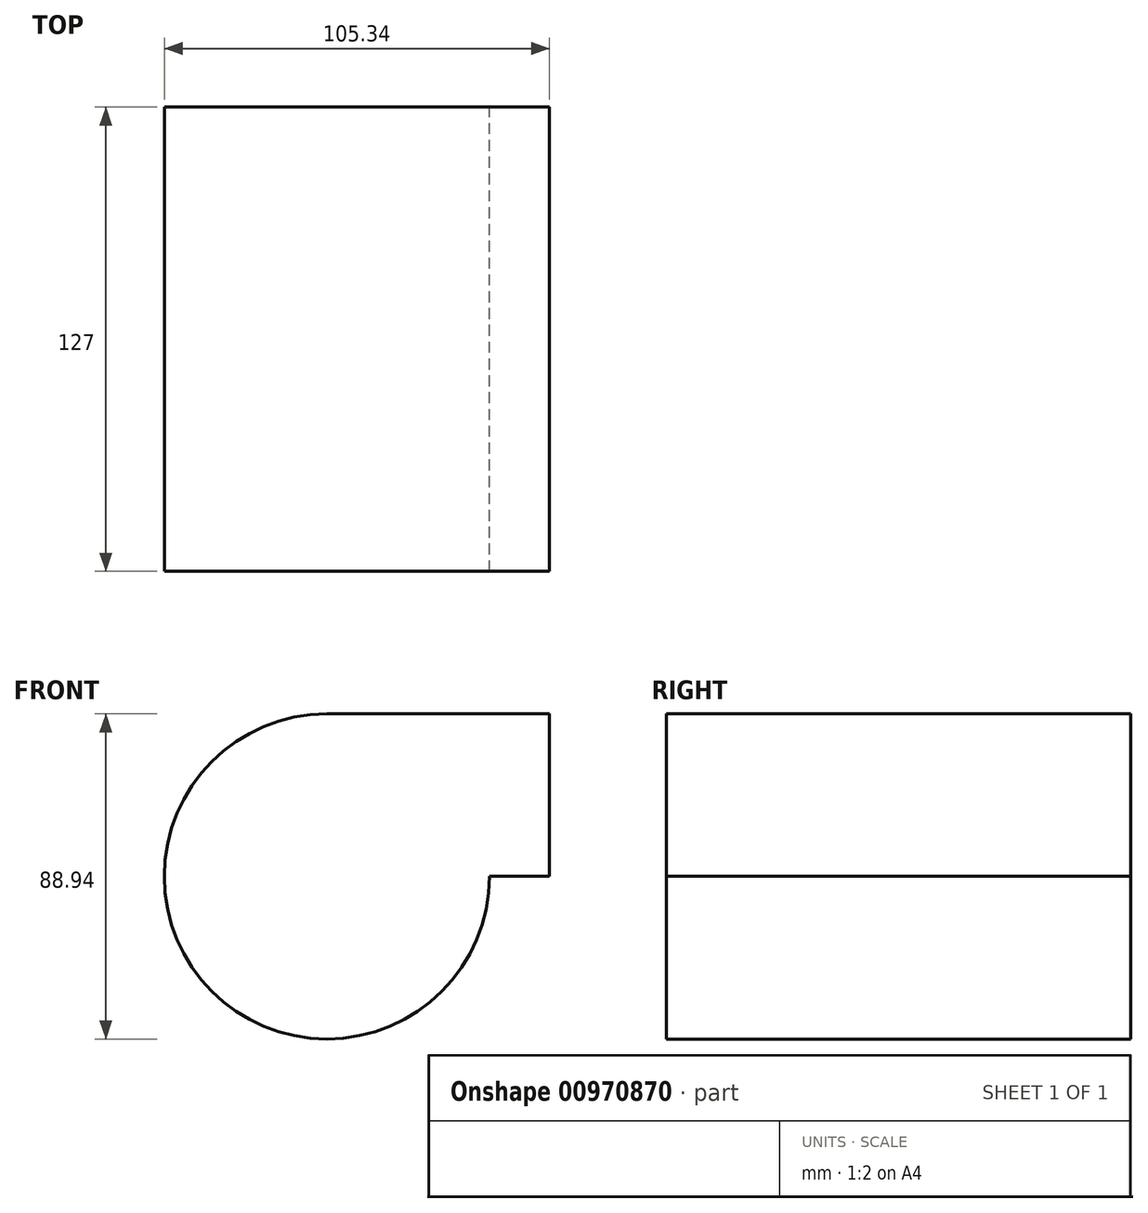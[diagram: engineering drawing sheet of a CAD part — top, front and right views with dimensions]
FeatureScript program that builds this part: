
annotation { "Feature Type Name" : "Feature", "Feature Type Description" : "" }
export const myFeature = defineFeature(function(context is Context, id is Id, definition is map)
    precondition{}
    {
        {
            var Q0;
            Q0=qCreatedBy(makeId("Front.planeOp"),FACE);
            var sketch = newSketch(context, id + "F0", { "sketchPlane" : qUnion([Q0])});
            skLineSegment(sketch, "E0", {"start": v(0, 44.47) * mm, "end": v(60.87, 44.47) * mm});
            skLineSegment(sketch, "E1", {"start": v(60.87, 44.47) * mm, "end": v(60.87, 0) * mm});
            skLineSegment(sketch, "E2", {"start": v(60.87, 0) * mm, "end": v(44.47, 0) * mm});
            skArc(sketch, "E3", {"start": v(0, 44.47) * mm, "mid": v(-31.44, -31.44) * mm, "end": v(44.47, 0) * mm});
            skSolve(sketch);
        }
        {
            var Q0;
            Q0 = qSketchRegion(id + "F0", true);
            extrude(context, id + "F1", {"entities" : qUnion([Q0]), "depth" : 25.4 * mm, "offsetDistance" : 25.4 * mm});
        }
        {
            var Q0;
            Q0 = qSketchRegion(id + "F0", true);
            extrude(context, id + "F2", {"entities" : qUnion([Q0]), "operationType" : NewBodyOperationType.ADD, "depth" : 127 * mm, "offsetDistance" : 25.4 * mm});
        }
    });
